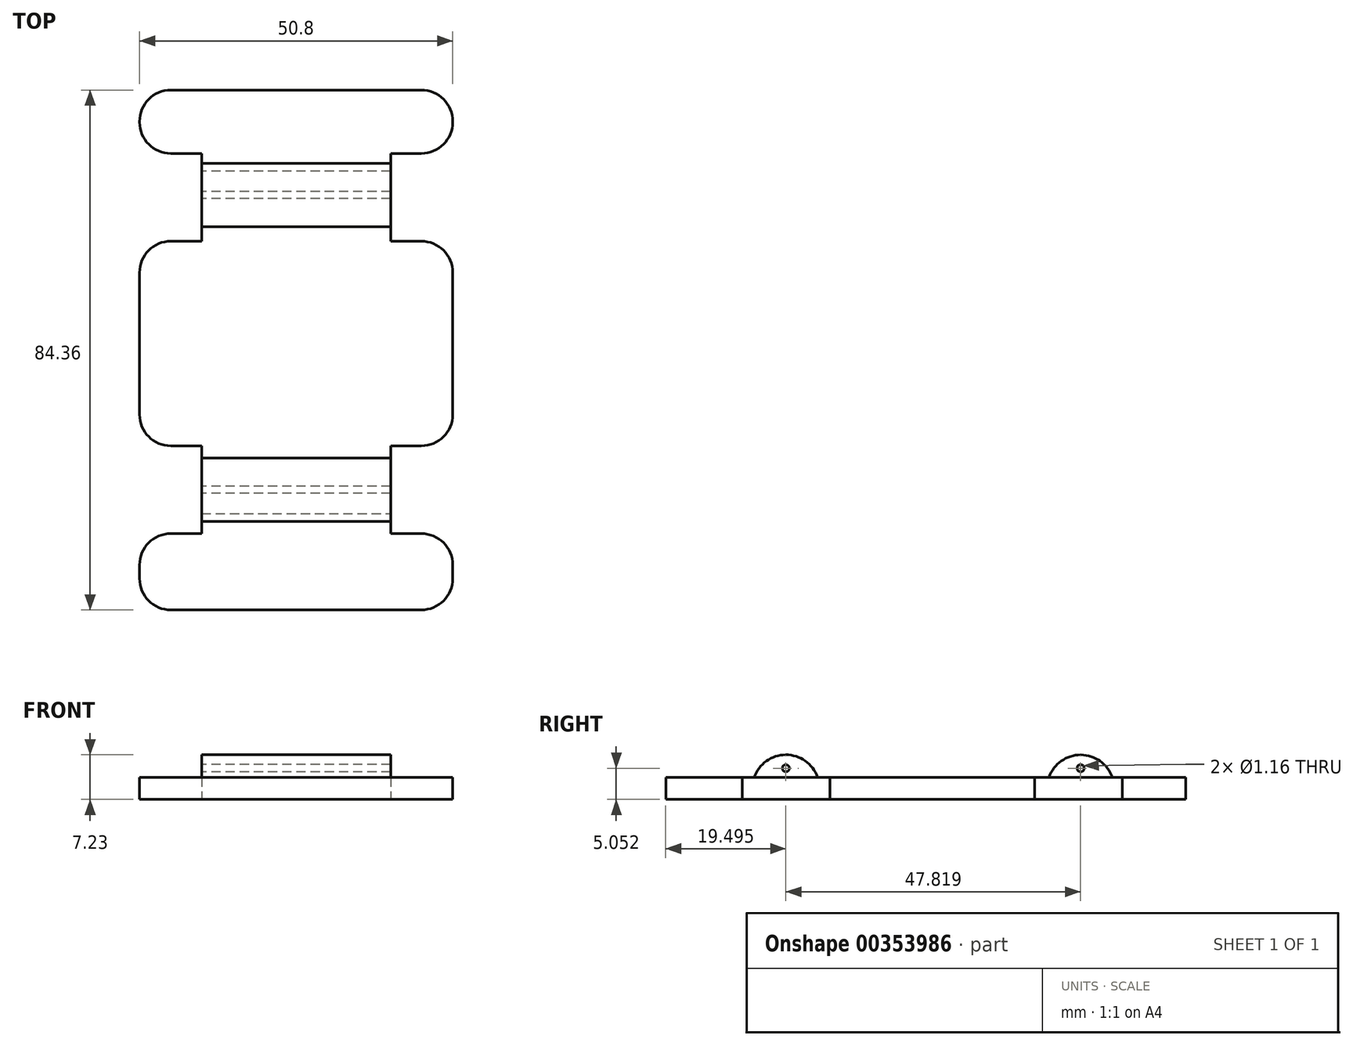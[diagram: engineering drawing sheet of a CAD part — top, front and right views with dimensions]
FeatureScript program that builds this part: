
annotation { "Feature Type Name" : "Feature", "Feature Type Description" : "" }
export const myFeature = defineFeature(function(context is Context, id is Id, definition is map)
    precondition{}
    {
        {
            var Q0;
            Q0=qCreatedBy(makeId("Top.planeOp"),FACE);
            var sketch = newSketch(context, id + "F0", { "sketchPlane" : qUnion([Q0])});
            skLineSegment(sketch, "E0.bottom", {"start": v(25.4, -42.18) * mm, "end": v(-25.4, -42.18) * mm});
            skLineSegment(sketch, "E0.top", {"start": v(25.4, 42.18) * mm, "end": v(-25.4, 42.18) * mm});
            skLineSegment(sketch, "E0.left", {"start": v(25.4, -42.18) * mm, "end": v(25.4, -29.8) * mm});
            skLineSegment(sketch, "E0.right", {"start": v(-25.4, -42.18) * mm, "end": v(-25.4, -29.8) * mm});
            skPoint(sketch, "E0.middle", {"position": v(0, 0) * mm});
            skLineSegment(sketch, "E1", {"start": v(-25.4, 31.9) * mm, "end": v(-15.34, 31.9) * mm});
            skLineSegment(sketch, "E2", {"start": v(-15.34, 31.9) * mm, "end": v(-15.34, 17.66) * mm});
            skLineSegment(sketch, "E3", {"start": v(-15.34, 17.66) * mm, "end": v(-25.4, 17.66) * mm});
            skLineSegment(sketch, "E4", {"start": v(-25.4, -15.55) * mm, "end": v(-15.34, -15.55) * mm});
            skLineSegment(sketch, "E5", {"start": v(-15.34, -15.55) * mm, "end": v(-15.34, -29.8) * mm});
            skLineSegment(sketch, "E6", {"start": v(-15.34, -29.8) * mm, "end": v(-25.4, -29.8) * mm});
            skLineSegment(sketch, "E7", {"start": v(25.4, 31.9) * mm, "end": v(15.34, 31.9) * mm});
            skLineSegment(sketch, "E8", {"start": v(15.34, 31.9) * mm, "end": v(15.34, 17.66) * mm});
            skLineSegment(sketch, "E9", {"start": v(15.34, 17.66) * mm, "end": v(25.4, 17.66) * mm});
            skLineSegment(sketch, "E10", {"start": v(25.4, -15.55) * mm, "end": v(15.34, -15.55) * mm});
            skLineSegment(sketch, "E11", {"start": v(15.34, -15.55) * mm, "end": v(15.34, -29.8) * mm});
            skLineSegment(sketch, "E12", {"start": v(15.34, -29.8) * mm, "end": v(25.4, -29.8) * mm});
            skLineSegment(sketch, "E13.trimOffspring", {"start": v(-25.4, 31.9) * mm, "end": v(-25.4, 42.18) * mm});
            skLineSegment(sketch, "E14.trimOffspring", {"start": v(25.4, 31.9) * mm, "end": v(25.4, 42.18) * mm});
            skLineSegment(sketch, "E15.trimOffspring", {"start": v(25.4, -15.55) * mm, "end": v(25.4, 17.66) * mm});
            skLineSegment(sketch, "E16.trimOffspring", {"start": v(-25.4, -15.55) * mm, "end": v(-25.4, 17.66) * mm});
            skSolve(sketch);
        }
        {
            var Q0;
            Q0=makeQuery(id+"F0.imprint","IMPRINT",FACE,{"disambiguationData":[TD([[makeQuery(id+"F0.imprint","IMPRINT",EDGE,{"derivedFrom":sQuery(id+"F0.wireOp",EDGE,"E0.bottom")}),-1.0]])]});
            extrude(context, id + "F1", {"entities" : qUnion([Q0]), "endBound" : BoundingType.SYMMETRIC, "depth" : 3.56 * mm});
        }
        {
            var Q0;
            Q0=qCreatedBy(makeId("Right.planeOp"),FACE);
            var sketch = newSketch(context, id + "F2", { "sketchPlane" : qUnion([Q0])});
            skArc(sketch, "E17", {"start": v(-17.55, 1.8) * mm, "mid": v(-22.7, 5.45) * mm, "end": v(-27.83, 1.77) * mm});
            skArc(sketch, "E18", {"start": v(30.28, 1.77) * mm, "mid": v(25.15, 5.44) * mm, "end": v(20, 1.8) * mm});
            skCircle(sketch, "E19", {"center": v(25.13, 3.27) * mm, "radius": 0.58 * mm});
            skCircle(sketch, "E20", {"center": v(-22.69, 3.27) * mm, "radius": 0.58 * mm});
            skLineSegment(sketch, "E21", {"start": v(-27.83, 1.77) * mm, "end": v(-17.55, 1.8) * mm});
            skLineSegment(sketch, "E22", {"start": v(20, 1.8) * mm, "end": v(30.28, 1.77) * mm});
            skSolve(sketch);
        }
        {
            var Q0;
            Q0 = qSketchRegion(id + "F2", true);
            extrude(context, id + "F3", {"entities" : qUnion([Q0]), "operationType" : NewBodyOperationType.ADD, "endBound" : BoundingType.SYMMETRIC, "depth" : 30.68 * mm});
        }
        {
            var Q0;
            Q0=makeQuery(id+"F1.opExtrude","SWEPT_EDGE",EDGE,{"disambiguationData":[OSD([sQuery(id+"F0.wireOp",EDGE,"E0.bottom"),sQuery(id+"F0.wireOp",EDGE,"E0.left")])]});
            var Q1;
            Q1=makeQuery(id+"F1.opExtrude","SWEPT_EDGE",EDGE,{"disambiguationData":[OSD([sQuery(id+"F0.wireOp",EDGE,"E0.bottom"),sQuery(id+"F0.wireOp",EDGE,"E0.right")])]});
            var Q2;
            Q2=makeQuery(id+"F1.opExtrude","SWEPT_EDGE",EDGE,{"disambiguationData":[OSD([sQuery(id+"F0.wireOp",EDGE,"E0.right"),sQuery(id+"F0.wireOp",EDGE,"E6")])]});
            var Q3;
            Q3=makeQuery(id+"F1.opExtrude","SWEPT_EDGE",EDGE,{"disambiguationData":[OSD([sQuery(id+"F0.wireOp",EDGE,"E4"),sQuery(id+"F0.wireOp",EDGE,"E16.trimOffspring")])]});
            var Q4;
            Q4=makeQuery(id+"F1.opExtrude","SWEPT_EDGE",EDGE,{"disambiguationData":[OSD([sQuery(id+"F0.wireOp",EDGE,"E3"),sQuery(id+"F0.wireOp",EDGE,"E16.trimOffspring")])]});
            var Q5;
            Q5=makeQuery(id+"F1.opExtrude","SWEPT_EDGE",EDGE,{"disambiguationData":[OSD([sQuery(id+"F0.wireOp",EDGE,"E1"),sQuery(id+"F0.wireOp",EDGE,"E13.trimOffspring")])]});
            var Q6;
            Q6=makeQuery(id+"F1.opExtrude","SWEPT_EDGE",EDGE,{"disambiguationData":[OSD([sQuery(id+"F0.wireOp",EDGE,"E0.top"),sQuery(id+"F0.wireOp",EDGE,"E13.trimOffspring")])]});
            var Q7;
            Q7=makeQuery(id+"F1.opExtrude","SWEPT_EDGE",EDGE,{"disambiguationData":[OSD([sQuery(id+"F0.wireOp",EDGE,"E0.top"),sQuery(id+"F0.wireOp",EDGE,"E14.trimOffspring")])]});
            var Q8;
            Q8=makeQuery(id+"F1.opExtrude","SWEPT_EDGE",EDGE,{"disambiguationData":[OSD([sQuery(id+"F0.wireOp",EDGE,"E9"),sQuery(id+"F0.wireOp",EDGE,"E15.trimOffspring")])]});
            var Q9;
            Q9=makeQuery(id+"F1.opExtrude","SWEPT_EDGE",EDGE,{"disambiguationData":[OSD([sQuery(id+"F0.wireOp",EDGE,"E7"),sQuery(id+"F0.wireOp",EDGE,"E14.trimOffspring")])]});
            var Q10;
            Q10=makeQuery(id+"F1.opExtrude","SWEPT_EDGE",EDGE,{"disambiguationData":[OSD([sQuery(id+"F0.wireOp",EDGE,"E0.left"),sQuery(id+"F0.wireOp",EDGE,"E12")])]});
            var Q11;
            Q11=makeQuery(id+"F1.opExtrude","SWEPT_EDGE",EDGE,{"disambiguationData":[OSD([sQuery(id+"F0.wireOp",EDGE,"E10"),sQuery(id+"F0.wireOp",EDGE,"E15.trimOffspring")])]});
            fillet(context, id + "F4", {"entities" : qUnion([Q0, Q1, Q2, Q3, Q4, Q5, Q6, Q7, Q8, Q9, Q10, Q11]), "radius" : 5.08 * mm, "tangentPropagation" : true, "allowEdgeOverflow" : false});
        }
    });
